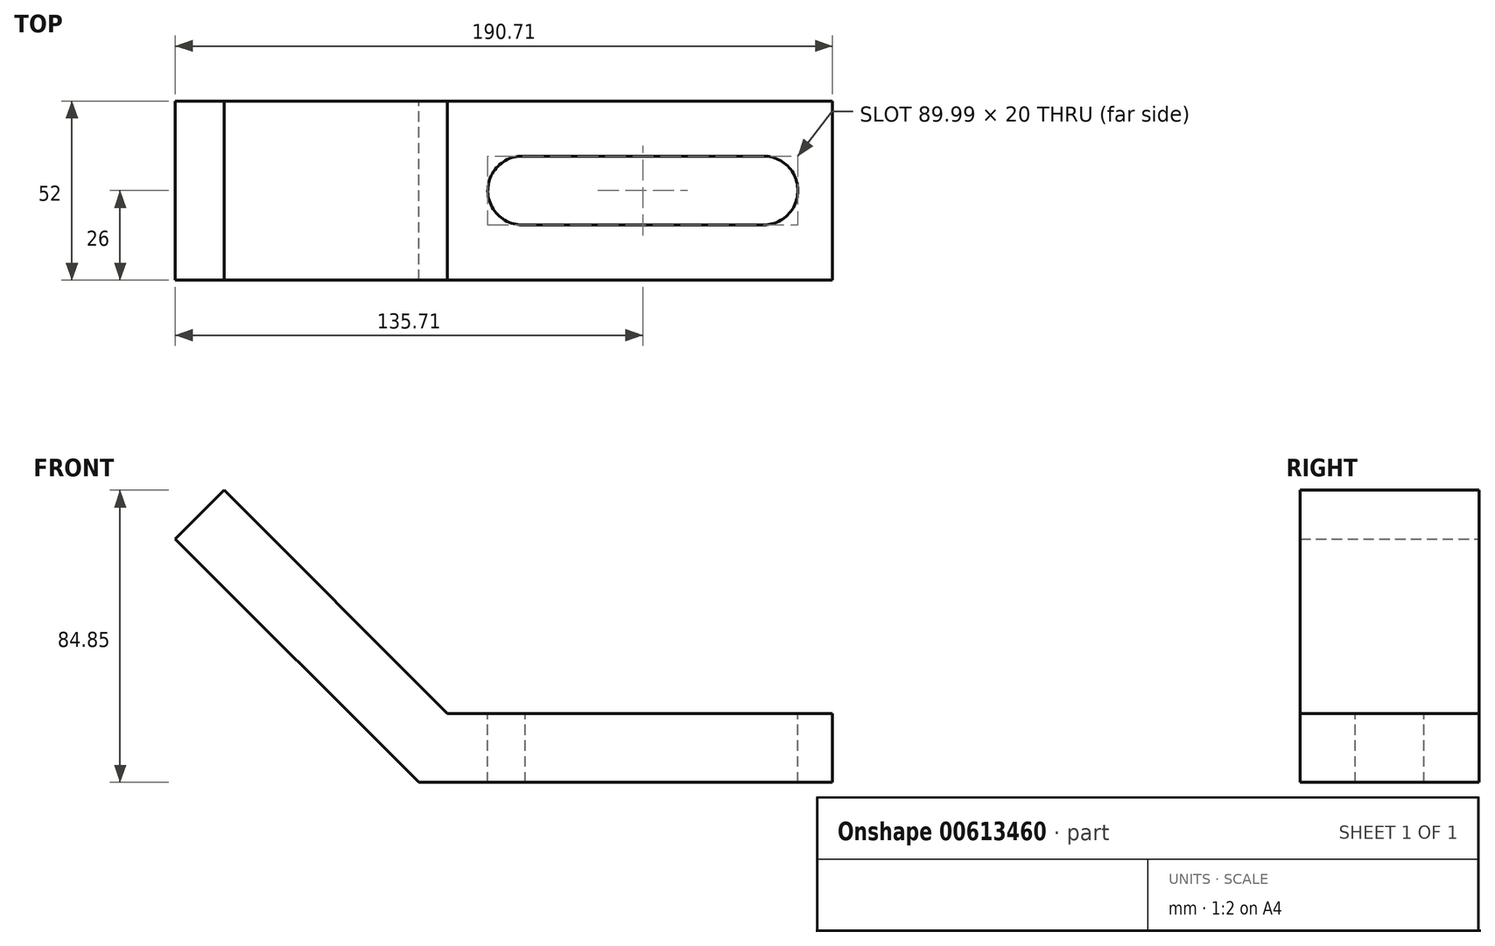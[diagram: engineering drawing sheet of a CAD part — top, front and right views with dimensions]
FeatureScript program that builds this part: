
annotation { "Feature Type Name" : "Feature", "Feature Type Description" : "" }
export const myFeature = defineFeature(function(context is Context, id is Id, definition is map)
    precondition{}
    {
        {
            var Q0;
            Q0=qCreatedBy(makeId("Front.planeOp"),FACE);
            var sketch = newSketch(context, id + "F0", { "sketchPlane" : qUnion([Q0])});
            skLineSegment(sketch, "E0", {"start": v(-64.85, 64.85) * mm, "end": v(0, 0) * mm});
            skLineSegment(sketch, "E1", {"start": v(111.72, 0) * mm, "end": v(0, 0) * mm});
            skLineSegment(sketch, "E2", {"start": v(-64.85, 64.85) * mm, "end": v(-79, 50.71) * mm});
            skLineSegment(sketch, "E3", {"start": v(-79, 50.71) * mm, "end": v(-8.28, -20) * mm});
            skLineSegment(sketch, "E4", {"start": v(-8.28, -20) * mm, "end": v(111.72, -20) * mm});
            skLineSegment(sketch, "E5", {"start": v(111.72, -20) * mm, "end": v(111.72, 0) * mm});
            skSolve(sketch);
        }
        {
            var Q0;
            Q0=makeQuery(id+"F0.imprint","IMPRINT",FACE,{"disambiguationData":[TD([[makeQuery(id+"F0.imprint","IMPRINT",EDGE,{"derivedFrom":sQuery(id+"F0.wireOp",EDGE,"E0")}),-1.0]])]});
            extrude(context, id + "F1", {"entities" : qUnion([Q0]), "depth" : 52 * mm, "offsetDistance" : 25 * mm});
        }
        {
            var Q0;
            Q0=makeQuery(id+"F1.opExtrude","SWEPT_FACE",FACE,{"disambiguationData":[OSD([sQuery(id+"F0.wireOp",EDGE,"E1")])]});
            var sketch = newSketch(context, id + "F2", { "sketchPlane" : qUnion([Q0])});
            skArc(sketch, "E6", {"start": v(91.72, -36) * mm, "mid": v(101.72, -26) * mm, "end": v(91.7, -16) * mm});
            skArc(sketch, "E7", {"start": v(22.62, -16.04) * mm, "mid": v(11.72, -25.58) * mm, "end": v(21.8, -36) * mm});
            skLineSegment(sketch, "E8", {"start": v(22.62, -16.04) * mm, "end": v(91.7, -16) * mm});
            skLineSegment(sketch, "E9", {"start": v(21.8, -36) * mm, "end": v(91.72, -36) * mm});
            skSolve(sketch);
        }
        {
            var Q0;
            Q0=makeQuery(id+"F2.imprint","IMPRINT",FACE,{"disambiguationData":[TD([[makeQuery(id+"F2.imprint","IMPRINT",EDGE,{"derivedFrom":sQuery(id+"F2.wireOp",EDGE,"E6")}),1.0]])]});
            extrude(context, id + "F3", {"entities" : qUnion([Q0]), "operationType" : NewBodyOperationType.REMOVE, "endBound" : BoundingType.UP_TO_NEXT, "oppositeDirection" : true, "depth" : 25 * mm, "offsetDistance" : 25 * mm});
        }
        {
            var Q0;
            Q0=makeQuery(id+"F1.opExtrude","SWEPT_FACE",FACE,{"disambiguationData":[OSD([sQuery(id+"F0.wireOp",EDGE,"E0")])]});
            var sketch = newSketch(context, id + "F4", { "sketchPlane" : qUnion([Q0])});
            skArc(sketch, "E10", {"start": v(-65.72, 0) * mm, "mid": v(-91.72, -26) * mm, "end": v(-65.72, -52) * mm});
            skCircle(sketch, "E11", {"center": v(-65.72, -26) * mm, "radius": 10 * mm});
            skSolve(sketch);
        }
        {
            var Q0;
            {var subQ0=sQuery(id+"F4.wireOp",EDGE,"E10");var subQ1=sQuery(id+"F0.wireOp",EDGE,"E0");var subQ2=makeQuery(id+"F1.opExtrude","CAP_EDGE",EDGE,{"disambiguationData":[OSD([subQ1])],"isStart":false});var subQ3=makeQuery(id+"F4.imprint","INTERSECT",VERTEX,{"derivedFrom":[subQ2,subQ0]});Q0=makeQuery(id+"F4.imprint","IMPRINT",FACE,{"disambiguationData":[TD([[makeQuery(id+"F4.imprint","IMPRINT",EDGE,{"disambiguationData":[TD([[subQ3,1.0]])],"derivedFrom":subQ0}),-1.0]])]});}
            var Q1;
            Q1=makeQuery(id+"F4.imprint","IMPRINT",FACE,{"disambiguationData":[TD([[makeQuery(id+"F4.imprint","IMPRINT",EDGE,{"derivedFrom":sQuery(id+"F4.wireOp",EDGE,"E11")}),1.0]])]});
            var Q2;
            {var subQ0=sQuery(id+"F4.wireOp",EDGE,"E10");var subQ1=sQuery(id+"F0.wireOp",EDGE,"E0");var subQ2=makeQuery(id+"F1.opExtrude","CAP_EDGE",EDGE,{"disambiguationData":[OSD([subQ1])],"isStart":true});var subQ3=makeQuery(id+"F4.imprint","INTERSECT",VERTEX,{"derivedFrom":[subQ2,subQ0]});Q2=makeQuery(id+"F4.imprint","IMPRINT",FACE,{"disambiguationData":[TD([[makeQuery(id+"F4.imprint","IMPRINT",EDGE,{"disambiguationData":[TD([[subQ3,-1.0]])],"derivedFrom":subQ0}),-1.0]])]});}
            extrude(context, id + "F5", {"entities" : qUnion([Q0, Q1, Q2]), "operationType" : NewBodyOperationType.REMOVE, "oppositeDirection" : true, "depth" : 25 * mm, "offsetDistance" : 25 * mm});
        }
    });
